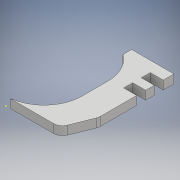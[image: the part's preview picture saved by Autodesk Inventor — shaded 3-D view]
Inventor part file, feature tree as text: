
AUTODESK INVENTOR PART (.ipt)
format: ipt  version: 2017 (Build 210142000, 142)  size: 159,232 bytes
history: native  units: mm
features: sketch x5, extrude x3, hole x1
ambient origin geometry x8: Origin, YZ Plane, XZ Plane, XY Plane, X Axis, Y Axis, Z Axis, Center Point
bodies: Solid1 (feature_tree)
feature tree (9):
  sketch  "Sketch1"  dims[d0=22.0mm d1=90.0deg]
  sketch  "Sketch2"  dims[d2=0.0mm d3=15.0mm]
  extrude  "Extrusion1"  TaperAngle=90.0deg  [1 undecoded]
  hole  "Hole1"  [1 undecoded]
  extrude  "Extrusion2"  Depth=13.0mm
  extrude  "Extrusion3"  Depth=22.0mm
  sketch  "Sketch3"  dims[d4=0.0mm d5=13.0mm]
  sketch  "Sketch4"  dims[d6=22.0mm d7=12.0mm]
  sketch  "Sketch5"  dims[d8=22.5mm d9=15.0mm d10=90.0mm d11=37.0mm d12=5.0mm d13=12.124057mm d14=5.2mm d15=5.2mm d16=5.0mm d17=7.5mm d18=5.0mm d19=0.0mm d20=18.0mm d21=7.5mm d22=7.5mm d23=3.5mm d24=3.4mm d25=6.0mm d26=4.0mm d27=2.0mm d28=90.0deg d29=8.0mm d30=20.594885mm d31=0.0mm d32=15.0mm d33=0.0mm d34=7.0mm d35=40.0mm d36=0.0mm]
note: 2 required parameter values undecoded (feature->parameter linkage not recoverable at this tier; creation-order binding heuristic only, values carry confidence <= 0.55)
